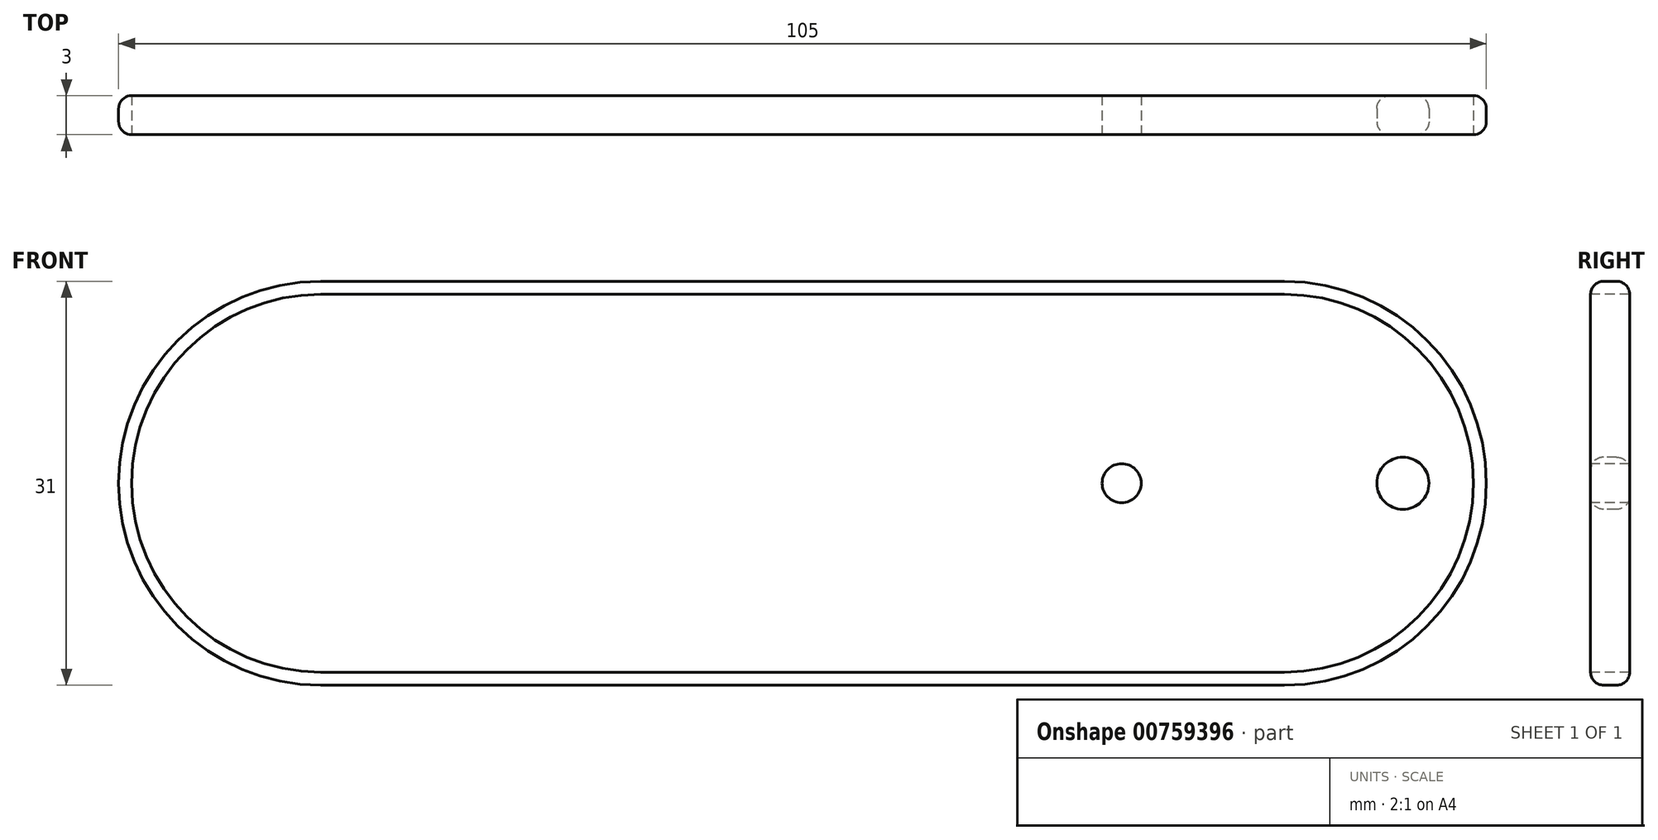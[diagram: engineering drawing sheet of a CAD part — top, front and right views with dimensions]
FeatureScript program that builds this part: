
annotation { "Feature Type Name" : "Feature", "Feature Type Description" : "" }
export const myFeature = defineFeature(function(context is Context, id is Id, definition is map)
    precondition{}
    {
        {
            var Q0;
            Q0=qCreatedBy(makeId("Front.planeOp"),FACE);
            var sketch = newSketch(context, id + "F0", { "sketchPlane" : qUnion([Q0])});
            skLineSegment(sketch, "E0.bottom", {"start": v(-37, 15.5) * mm, "end": v(37, 15.5) * mm});
            skLineSegment(sketch, "E0.top", {"start": v(-37, -15.5) * mm, "end": v(37, -15.5) * mm});
            skLineSegment(sketch, "E0.left", {"start": v(-52.5, 0) * mm, "end": v(-52.5, 0) * mm});
            skLineSegment(sketch, "E0.right", {"start": v(52.5, 0) * mm, "end": v(52.5, 0) * mm});
            skPoint(sketch, "E0.middle", {"position": v(0, 0) * mm});
            skPoint(sketch, "E1.visualSharp", {"position": v(-52.5, 15.5) * mm});
            skArc(sketch, "E1.filletArc", {"start": v(-37, 15.5) * mm, "mid": v(-47.96, 10.96) * mm, "end": v(-52.5, 0) * mm});
            skPoint(sketch, "E2.visualSharp", {"position": v(-52.5, -15.5) * mm});
            skArc(sketch, "E2.filletArc", {"start": v(-52.5, 0) * mm, "mid": v(-47.96, -10.96) * mm, "end": v(-37, -15.5) * mm});
            skPoint(sketch, "E3.visualSharp", {"position": v(52.5, -15.5) * mm});
            skArc(sketch, "E3.filletArc", {"start": v(37, -15.5) * mm, "mid": v(47.96, -10.96) * mm, "end": v(52.5, 0) * mm});
            skPoint(sketch, "E4.visualSharp", {"position": v(52.5, 15.5) * mm});
            skArc(sketch, "E4.filletArc", {"start": v(52.5, 0) * mm, "mid": v(47.96, 10.96) * mm, "end": v(37, 15.5) * mm});
            skSolve(sketch);
        }
        {
            var Q0;
            Q0=makeQuery(id+"F0.imprint","IMPRINT",FACE,{"disambiguationData":[TD([[makeQuery(id+"F0.imprint","IMPRINT",EDGE,{"derivedFrom":sQuery(id+"F0.wireOp",EDGE,"E0.bottom")}),-1.0]])]});
            extrude(context, id + "F1", {"entities" : qUnion([Q0]), "depth" : 3 * mm, "offsetDistance" : 25 * mm});
        }
        {
            var Q0;
            Q0=makeQuery(id+"F1.opExtrude","CAP_EDGE",EDGE,{"disambiguationData":[OSD([sQuery(id+"F0.wireOp",EDGE,"E1.filletArc"),sQuery(id+"F0.wireOp",EDGE,"E2.filletArc")])],"isStart":false});
            var Q1;
            Q1=makeQuery(id+"F1.opExtrude","CAP_EDGE",EDGE,{"disambiguationData":[OSD([sQuery(id+"F0.wireOp",EDGE,"E0.top")])],"isStart":false});
            fillet(context, id + "F2", {"entities" : qUnion([Q0, Q1]), "radius" : 1 * mm, "tangentPropagation" : true, "allowEdgeOverflow" : false});
        }
        {
            var Q0;
            Q0=makeQuery(id+"F1.opExtrude","CAP_FACE",FACE,{"disambiguationData":[OSD([sQuery(id+"F0.wireOp",EDGE,"E0.bottom"),sQuery(id+"F0.wireOp",EDGE,"E0.top"),sQuery(id+"F0.wireOp",EDGE,"E1.filletArc"),sQuery(id+"F0.wireOp",EDGE,"E2.filletArc"),sQuery(id+"F0.wireOp",EDGE,"E3.filletArc"),sQuery(id+"F0.wireOp",EDGE,"E4.filletArc")])],"isStart":false});
            var sketch = newSketch(context, id + "F3", { "sketchPlane" : qUnion([Q0])});
            skCircle(sketch, "E5", {"center": v(-46.09, 0) * mm, "radius": 2 * mm});
            skCircle(sketch, "E6", {"center": v(-24.5, 0) * mm, "radius": 1.5 * mm});
            skCircle(sketch, "E7.MirrorC", {"center": v(46.09, 0) * mm, "radius": 2 * mm});
            skCircle(sketch, "E8.MirrorC", {"center": v(24.5, 0) * mm, "radius": 1.5 * mm});
            skPoint(sketch, "E9.center.orphan", {"position": v(31.2, 0) * mm});
            skPoint(sketch, "E10.center.orphan", {"position": v(22.07, 0) * mm});
            skSolve(sketch);
        }
        {
            var Q0;
            Q0=makeQuery(id+"F3.imprint","IMPRINT",FACE,{"disambiguationData":[TD([[makeQuery(id+"F3.imprint","IMPRINT",EDGE,{"derivedFrom":sQuery(id+"F3.wireOp",EDGE,"E5")}),1.0]])]});
            var Q1;
            Q1=makeQuery(id+"F3.imprint","IMPRINT",FACE,{"disambiguationData":[TD([[makeQuery(id+"F3.imprint","IMPRINT",EDGE,{"derivedFrom":sQuery(id+"F3.wireOp",EDGE,"E7.MirrorC")}),-1.0]])]});
            extrude(context, id + "F4", {"entities" : qUnion([Q0, Q1]), "operationType" : NewBodyOperationType.REMOVE, "oppositeDirection" : true, "depth" : 25 * mm, "offsetDistance" : 25 * mm});
        }
        {
            var Q0;
            Q0=makeQuery(id+"F3.imprint","IMPRINT",FACE,{"disambiguationData":[TD([[makeQuery(id+"F3.imprint","IMPRINT",EDGE,{"derivedFrom":sQuery(id+"F3.wireOp",EDGE,"E8.MirrorC")}),-1.0]])]});
            var Q1;
            Q1=makeQuery(id+"F3.imprint","IMPRINT",FACE,{"disambiguationData":[TD([[makeQuery(id+"F3.imprint","IMPRINT",EDGE,{"derivedFrom":sQuery(id+"F3.wireOp",EDGE,"E6")}),1.0]])]});
            extrude(context, id + "F5", {"entities" : qUnion([Q0, Q1]), "operationType" : NewBodyOperationType.REMOVE, "oppositeDirection" : true, "depth" : 25 * mm, "offsetDistance" : 25 * mm});
        }
        {
            var Q0;
            Q0=makeQuery(id+"F4.boolean.opBoolean","COPY",EDGE,{"derivedFrom":makeQuery(id+"F4.opExtrude","CAP_EDGE",EDGE,{"disambiguationData":[OSD([sQuery(id+"F3.wireOp",EDGE,"E5")])],"isStart":true})});
            var Q1;
            Q1=makeQuery(id+"F4.boolean.opBoolean","COPY",EDGE,{"derivedFrom":makeQuery(id+"F4.opExtrude","CAP_EDGE",EDGE,{"disambiguationData":[OSD([sQuery(id+"F3.wireOp",EDGE,"E7.MirrorC")])],"isStart":true})});
            var Q2;
            Q2=makeQuery(id+"F4.boolean.opBoolean","INTERSECT",EDGE,{"derivedFrom":[makeQuery(id+"F1.opExtrude","CAP_FACE",FACE,{"disambiguationData":[OSD([sQuery(id+"F0.wireOp",EDGE,"E0.bottom"),sQuery(id+"F0.wireOp",EDGE,"E0.top"),sQuery(id+"F0.wireOp",EDGE,"E1.filletArc"),sQuery(id+"F0.wireOp",EDGE,"E2.filletArc"),sQuery(id+"F0.wireOp",EDGE,"E3.filletArc"),sQuery(id+"F0.wireOp",EDGE,"E4.filletArc")])],"isStart":true}),makeQuery(id+"F4.opExtrude","SWEPT_FACE",FACE,{"disambiguationData":[OSD([sQuery(id+"F3.wireOp",EDGE,"E7.MirrorC")])]})]});
            var Q3;
            Q3=makeQuery(id+"F4.boolean.opBoolean","INTERSECT",EDGE,{"derivedFrom":[makeQuery(id+"F1.opExtrude","CAP_FACE",FACE,{"disambiguationData":[OSD([sQuery(id+"F0.wireOp",EDGE,"E0.bottom"),sQuery(id+"F0.wireOp",EDGE,"E0.top"),sQuery(id+"F0.wireOp",EDGE,"E1.filletArc"),sQuery(id+"F0.wireOp",EDGE,"E2.filletArc"),sQuery(id+"F0.wireOp",EDGE,"E3.filletArc"),sQuery(id+"F0.wireOp",EDGE,"E4.filletArc")])],"isStart":true}),makeQuery(id+"F4.opExtrude","SWEPT_FACE",FACE,{"disambiguationData":[OSD([sQuery(id+"F3.wireOp",EDGE,"E5")])]})]});
            fillet(context, id + "F6", {"entities" : qUnion([Q0, Q1, Q2, Q3]), "radius" : 1 * mm, "tangentPropagation" : true, "allowEdgeOverflow" : false});
        }
        {
            var Q0;
            Q0=makeQuery(id+"F1.opExtrude","CAP_EDGE",EDGE,{"disambiguationData":[OSD([sQuery(id+"F0.wireOp",EDGE,"E1.filletArc"),sQuery(id+"F0.wireOp",EDGE,"E2.filletArc")])],"isStart":true});
            fillet(context, id + "F7", {"entities" : qUnion([Q0]), "radius" : 1 * mm, "tangentPropagation" : true, "allowEdgeOverflow" : false});
        }
    });
